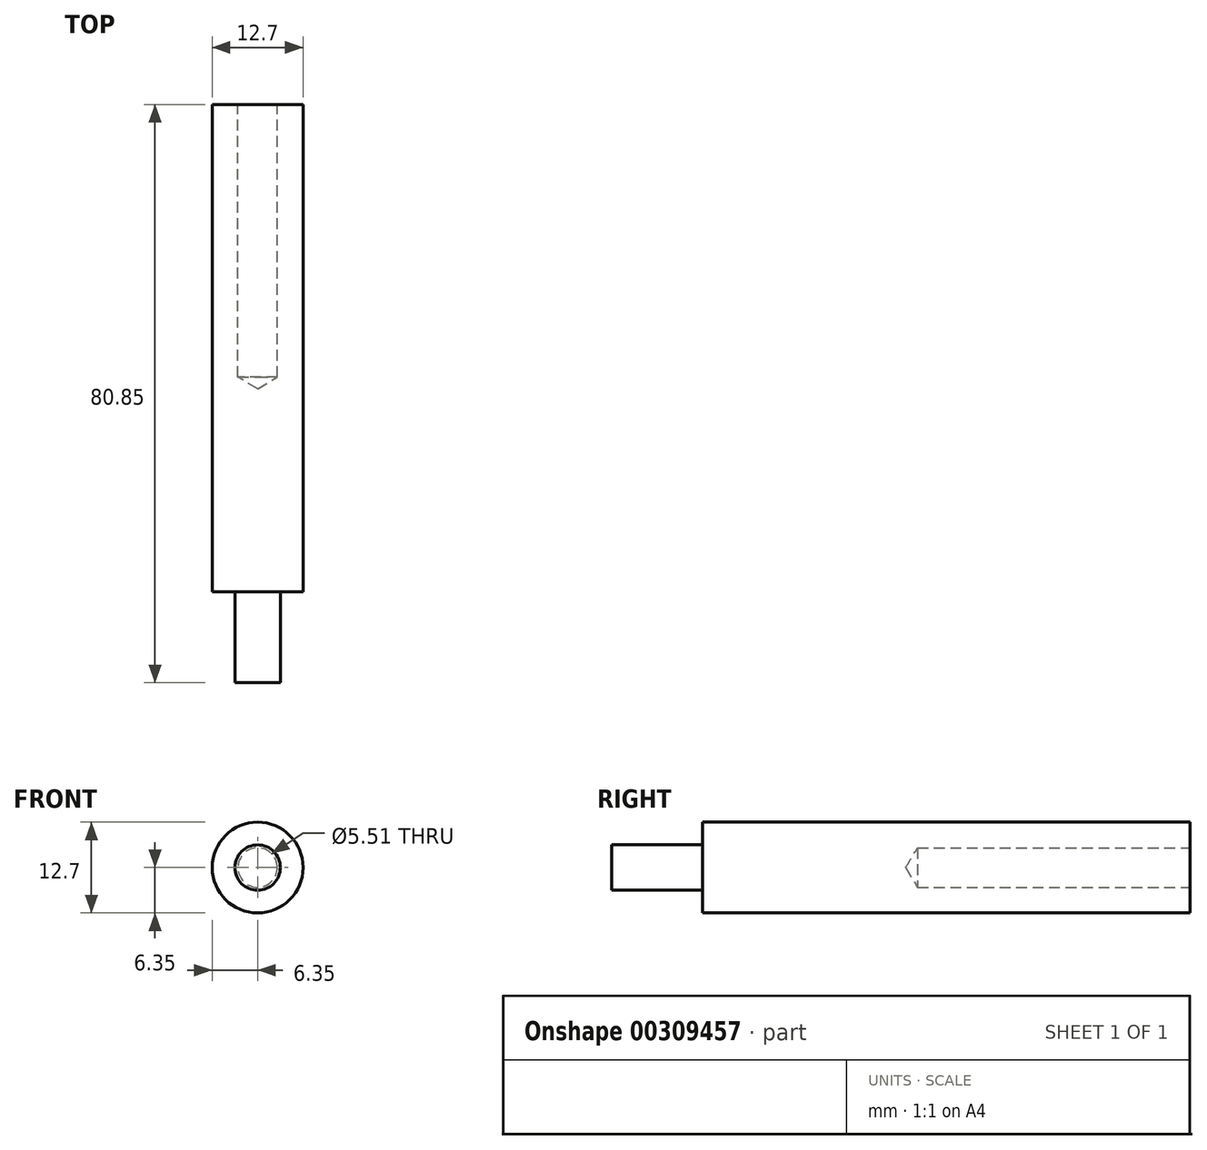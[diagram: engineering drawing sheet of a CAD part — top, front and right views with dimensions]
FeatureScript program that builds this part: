
annotation { "Feature Type Name" : "Feature", "Feature Type Description" : "" }
export const myFeature = defineFeature(function(context is Context, id is Id, definition is map)
    precondition{}
    {
        {
            var Q0;
            Q0=qCreatedBy(makeId("Front.planeOp"),FACE);
            var sketch = newSketch(context, id + "F0", { "sketchPlane" : qUnion([Q0])});
            skCircle(sketch, "E0", {"center": v(0, 0) * mm, "radius": 6.35 * mm});
            skSolve(sketch);
        }
        {
            var Q0;
            Q0 = qSketchRegion(id + "F0", true);
            extrude(context, id + "F1", {"entities" : qUnion([Q0]), "depth" : 93.55 * mm});
        }
        {
            var Q0;
            Q0=makeQuery(id+"F1.opExtrude","CAP_FACE",FACE,{"disambiguationData":[OSD([sQuery(id+"F0.wireOp",EDGE,"E0")])],"isStart":false});
            var sketch = newSketch(context, id + "F2", { "sketchPlane" : qUnion([Q0])});
            skCircle(sketch, "E1", {"center": v(0, 0) * mm, "radius": 3.18 * mm});
            skCircle(sketch, "E2", {"center": v(0, 0) * mm, "radius": 7.62 * mm});
            skSolve(sketch);
        }
        {
            var Q0;
            Q0 = qSketchRegion(id + "F2", true);
            extrude(context, id + "F3", {"entities" : qUnion([Q0]), "operationType" : NewBodyOperationType.REMOVE, "oppositeDirection" : true, "depth" : 12.7 * mm});
        }
        {
            var Q0;
            Q0=makeQuery(id+"F1.opExtrude","CAP_FACE",FACE,{"disambiguationData":[OSD([sQuery(id+"F0.wireOp",EDGE,"E0")])],"isStart":true});
            var sketch = newSketch(context, id + "F4", { "sketchPlane" : qUnion([Q0])});
            skPoint(sketch, "E3", {"position": v(0, 0) * mm});
            skSolve(sketch);
        }
        {
            var Q0;
            Q0=sQuery(id+"F4.wireOp",VERTEX,"E3");
            var Q1;
            Q1=makeQuery(id+"F1.opExtrude","SWEPT_BODY",BODY,{"disambiguationData":[OSD([sQuery(id+"F0.wireOp",EDGE,"E0")])]});
            hole(context, id + "F5", {"style" : HoleStyle.C_BORE, "endStyle" : HoleEndStyle.BLIND, "holeDiameter" : 5.5 * mm, "cBoreDiameter" : 12.7 * mm, "cBoreDepth" : 12.7 * mm, "holeDepth" : 50.8 * mm, "tappedDepth" : 12.7 * mm, "tapClearance" : 3, "locations" : qUnion([Q0]), "scope" : qUnion([Q1])});
        }
    });
